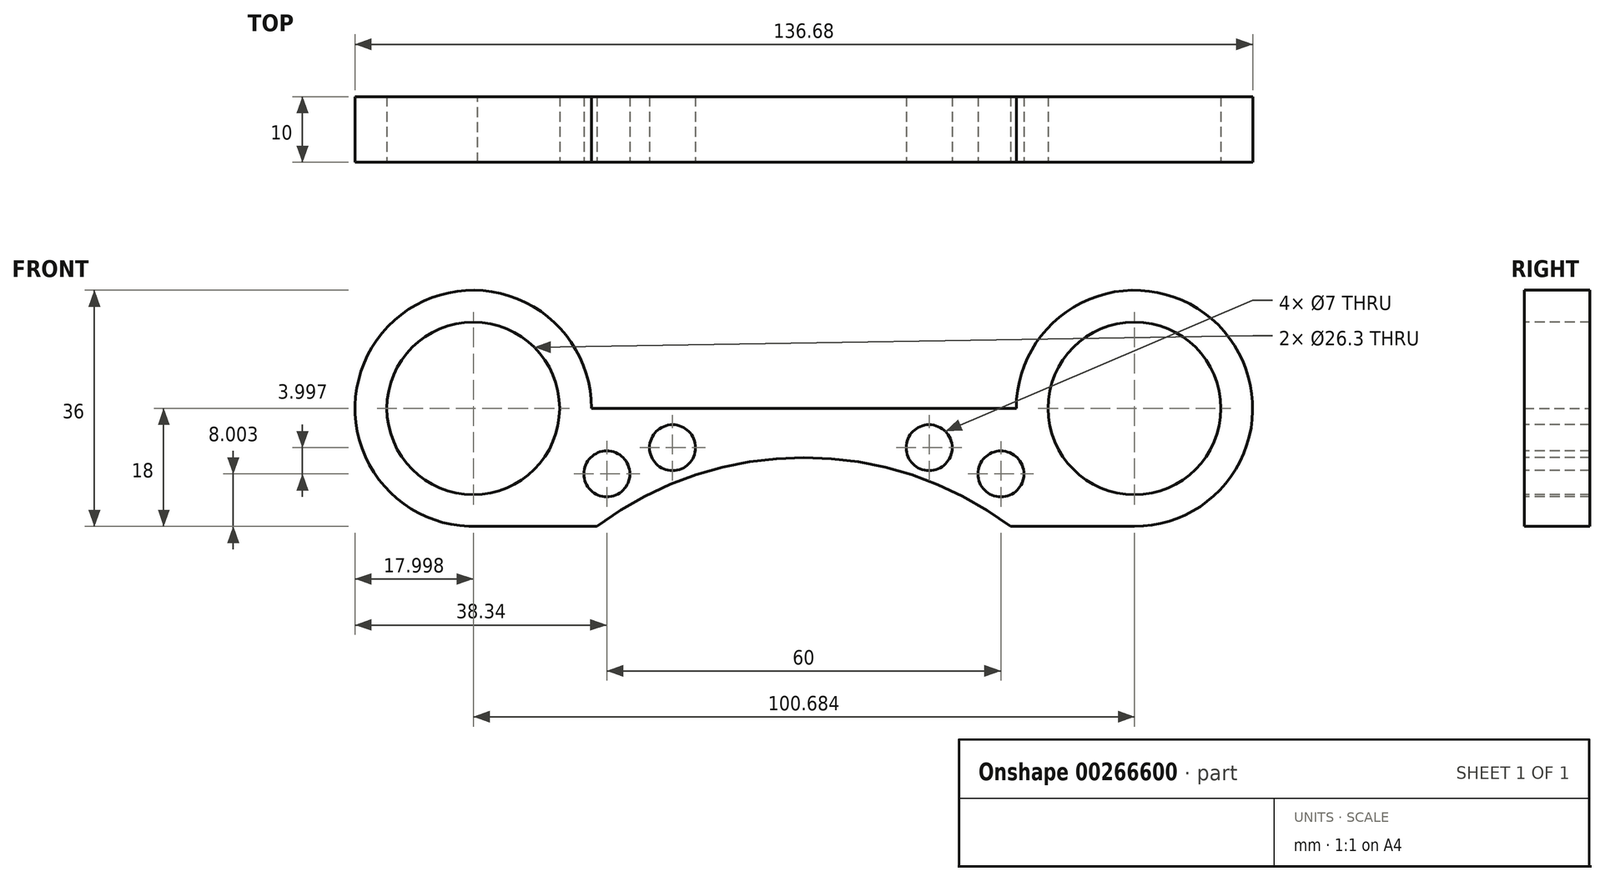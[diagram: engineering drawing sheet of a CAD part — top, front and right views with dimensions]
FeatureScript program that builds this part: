
annotation { "Feature Type Name" : "Feature", "Feature Type Description" : "" }
export const myFeature = defineFeature(function(context is Context, id is Id, definition is map)
    precondition{}
    {
        {
            var Q0;
            Q0=qCreatedBy(makeId("Front.planeOp"),FACE);
            var sketch = newSketch(context, id + "F0", { "sketchPlane" : qUnion([Q0])});
            skCircle(sketch, "E0", {"center": v(-50.34, 0) * mm, "radius": 18 * mm});
            skCircle(sketch, "E1", {"center": v(50.34, 0) * mm, "radius": 18 * mm});
            skLineSegment(sketch, "E2", {"start": v(-49.66, -17.99) * mm, "end": v(50.34, -18) * mm});
            skLineSegment(sketch, "E3", {"start": v(-32.34, 0) * mm, "end": v(32.34, 0) * mm});
            skSolve(sketch);
        }
        {
            var Q0;
            {var subQ0=sQuery(id+"F0.wireOp",EDGE,"E0");var subQ1=makeQuery(id+"F0.imprint","INTERSECT",VERTEX,{"derivedFrom":[subQ0,sQuery(id+"F0.wireOp",EDGE,"E2")]});Q0=makeQuery(id+"F0.imprint","IMPRINT",FACE,{"disambiguationData":[TD([[makeQuery(id+"F0.imprint","IMPRINT",EDGE,{"disambiguationData":[TD([[subQ1,1.0]])],"derivedFrom":subQ0}),1.0]])]});}
            var Q1;
            {var subQ0=sQuery(id+"F0.wireOp",EDGE,"E2");Q1=makeQuery(id+"F0.imprint","IMPRINT",FACE,{"disambiguationData":[TD([[makeQuery(id+"F0.imprint","IMPRINT",EDGE,{"derivedFrom":subQ0}),1.0]])]});}
            var Q2;
            {var subQ0=sQuery(id+"F0.wireOp",EDGE,"E1");var subQ1=makeQuery(id+"F0.imprint","INTERSECT",VERTEX,{"derivedFrom":[subQ0,sQuery(id+"F0.wireOp",EDGE,"E2")]});Q2=makeQuery(id+"F0.imprint","IMPRINT",FACE,{"disambiguationData":[TD([[makeQuery(id+"F0.imprint","IMPRINT",EDGE,{"disambiguationData":[TD([[subQ1,1.0]])],"derivedFrom":subQ0}),1.0]])]});}
            extrude(context, id + "F1", {"entities" : qUnion([Q0, Q1, Q2]), "depth" : 10 * mm});
        }
        {
            var Q0;
            Q0=makeQuery(id+"F1.opExtrude","CAP_FACE",FACE,{"disambiguationData":[OSD([sQuery(id+"F0.wireOp",EDGE,"E0"),sQuery(id+"F0.wireOp",EDGE,"E1"),sQuery(id+"F0.wireOp",EDGE,"E2"),sQuery(id+"F0.wireOp",EDGE,"E3")])],"isStart":false});
            var sketch = newSketch(context, id + "F2", { "sketchPlane" : qUnion([Q0])});
            skPoint(sketch, "E4", {"position": v(-50.34, 0) * mm});
            skPoint(sketch, "E5", {"position": v(50.34, 0) * mm});
            skCircle(sketch, "E6", {"center": v(-50.34, 0) * mm, "radius": 13.15 * mm});
            skCircle(sketch, "E7", {"center": v(50.34, 0) * mm, "radius": 13.15 * mm});
            skSolve(sketch);
        }
        {
            var Q0;
            Q0=makeQuery(id+"F2.imprint","IMPRINT",FACE,{"disambiguationData":[TD([[makeQuery(id+"F2.imprint","IMPRINT",EDGE,{"derivedFrom":sQuery(id+"F2.wireOp",EDGE,"E6")}),1.0]])]});
            var Q1;
            Q1=makeQuery(id+"F2.imprint","IMPRINT",FACE,{"disambiguationData":[TD([[makeQuery(id+"F2.imprint","IMPRINT",EDGE,{"derivedFrom":sQuery(id+"F2.wireOp",EDGE,"E7")}),1.0]])]});
            extrude(context, id + "F3", {"entities" : qUnion([Q0, Q1]), "operationType" : NewBodyOperationType.REMOVE, "oppositeDirection" : true, "depth" : 25 * mm});
        }
        {
            var Q0;
            Q0=makeQuery(id+"F1.opExtrude","CAP_FACE",FACE,{"disambiguationData":[OSD([sQuery(id+"F0.wireOp",EDGE,"E0"),sQuery(id+"F0.wireOp",EDGE,"E1"),sQuery(id+"F0.wireOp",EDGE,"E2"),sQuery(id+"F0.wireOp",EDGE,"E3")])],"isStart":false});
            var sketch = newSketch(context, id + "F4", { "sketchPlane" : qUnion([Q0])});
            skLineSegment(sketch, "E8", {"start": v(0, 0) * mm, "end": v(0, -60) * mm});
            skPoint(sketch, "E8.endSnap0", {"position": v(0, 0) * mm});
            skCircle(sketch, "E9", {"center": v(0, -60) * mm, "radius": 52.5 * mm});
            skSolve(sketch);
        }
        {
            var Q0;
            {var subQ0=sQuery(id+"F4.wireOp",EDGE,"E9");var subQ1=sQuery(id+"F4.wireOp",EDGE,"E8");var subQ2=makeQuery(id+"F4.imprint","INTERSECT",VERTEX,{"derivedFrom":[subQ1,subQ0]});Q0=makeQuery(id+"F4.imprint","IMPRINT",FACE,{"disambiguationData":[TD([[makeQuery(id+"F4.imprint","IMPRINT",EDGE,{"disambiguationData":[TD([[subQ2,-1.0]])],"derivedFrom":subQ1}),1.0]])]});}
            var Q1;
            {var subQ0=sQuery(id+"F4.wireOp",EDGE,"E9");var subQ1=sQuery(id+"F4.wireOp",EDGE,"E8");var subQ2=makeQuery(id+"F4.imprint","INTERSECT",VERTEX,{"derivedFrom":[subQ1,subQ0]});Q1=makeQuery(id+"F4.imprint","IMPRINT",FACE,{"disambiguationData":[TD([[makeQuery(id+"F4.imprint","IMPRINT",EDGE,{"disambiguationData":[TD([[subQ2,-1.0]])],"derivedFrom":subQ1}),-1.0]])]});}
            extrude(context, id + "F5", {"entities" : qUnion([Q0, Q1]), "operationType" : NewBodyOperationType.REMOVE, "endBound" : BoundingType.THROUGH_ALL, "oppositeDirection" : true, "depth" : 25 * mm});
        }
        {
            var Q0;
            Q0=makeQuery(id+"F1.opExtrude","CAP_FACE",FACE,{"disambiguationData":[OSD([sQuery(id+"F0.wireOp",EDGE,"E0"),sQuery(id+"F0.wireOp",EDGE,"E1"),sQuery(id+"F0.wireOp",EDGE,"E2"),sQuery(id+"F0.wireOp",EDGE,"E3")])],"isStart":false});
            var sketch = newSketch(context, id + "F6", { "sketchPlane" : qUnion([Q0])});
            skPoint(sketch, "E10", {"position": v(-30, -9.99) * mm});
            skPoint(sketch, "E11", {"position": v(30, -10) * mm});
            skCircle(sketch, "E12", {"center": v(-30, -9.99) * mm, "radius": 3.5 * mm});
            skCircle(sketch, "E13", {"center": v(30, -10) * mm, "radius": 3.5 * mm});
            skCircle(sketch, "E14", {"center": v(-20, -6) * mm, "radius": 3.5 * mm});
            skCircle(sketch, "E15", {"center": v(19.08, -6) * mm, "radius": 3.5 * mm});
            skSolve(sketch);
        }
        {
            var Q0;
            Q0=makeQuery(id+"F6.imprint","IMPRINT",FACE,{"disambiguationData":[TD([[makeQuery(id+"F6.imprint","IMPRINT",EDGE,{"derivedFrom":sQuery(id+"F6.wireOp",EDGE,"E12")}),1.0]])]});
            var Q1;
            Q1=makeQuery(id+"F6.imprint","IMPRINT",FACE,{"disambiguationData":[TD([[makeQuery(id+"F6.imprint","IMPRINT",EDGE,{"derivedFrom":sQuery(id+"F6.wireOp",EDGE,"E14")}),1.0]])]});
            var Q2;
            Q2=makeQuery(id+"F6.imprint","IMPRINT",FACE,{"disambiguationData":[TD([[makeQuery(id+"F6.imprint","IMPRINT",EDGE,{"derivedFrom":sQuery(id+"F6.wireOp",EDGE,"E15")}),1.0]])]});
            var Q3;
            Q3=makeQuery(id+"F6.imprint","IMPRINT",FACE,{"disambiguationData":[TD([[makeQuery(id+"F6.imprint","IMPRINT",EDGE,{"derivedFrom":sQuery(id+"F6.wireOp",EDGE,"E13")}),1.0]])]});
            extrude(context, id + "F7", {"entities" : qUnion([Q0, Q1, Q2, Q3]), "operationType" : NewBodyOperationType.REMOVE, "endBound" : BoundingType.THROUGH_ALL, "oppositeDirection" : true, "depth" : 25 * mm});
        }
    });
